# Revit family: Home collection grab rail - straight 900mm-687373C
name_source: partatom
category: Specialty Equipment
revit_build: Autodesk Revit 2015 (Build: 20140606_1530(x64)
units: mm (PartAtom-declared; Revit-internal decimal feet)

## types (8) — shared parameters
Assembly Code = C1030200
Default Elevation = 900 mm  [stored 2.95276 ft]
Manufacturer = GWA Bathrooms & Kitchens
URL = https://www.caroma.com.au

## per-type parameters (varying)
| type | Material_Rail | Model | Rail_Offset | Rail_Width |
| Home collection grab rail - straight 300mm Chrome | GWA_Metal-Chrome | 687370C | 76 mm  [stored 0.249344 ft] | 300 mm |
| Home collection grab rail - straight 300mm White | GWA-Metal-White | 687370W | 76 mm  [stored 0.249344 ft] | 300 mm |
| Home collection grab rail - straight 450mm Chrome | GWA_Metal-Chrome | 687371C | 76 mm  [stored 0.249344 ft] | 450 mm  [stored 1.47638 ft] |
| Home collection grab rail - straight 450mm White | GWA-Metal-White | 687371W | 76 mm  [stored 0.249344 ft] | 450 mm  [stored 1.47638 ft] |
| Home collection grab rail - straight 600mm Chrome | GWA_Metal-Chrome | 687372C | 71 mm  [stored 0.23294 ft] | 600 mm |
| Home collection grab rail - straight 600mm White | GWA-Metal-White | 687372W | 71 mm  [stored 0.23294 ft] | 600 mm |
| Home collection grab rail - straight 900mm Chrome | GWA_Metal-Chrome | 687373C | 71 mm  [stored 0.23294 ft] | 900 mm  [stored 2.95276 ft] |
| Home collection grab rail - straight 900mm White | GWA-Metal-White | 687373W | 71 mm  [stored 0.23294 ft] | 900 mm  [stored 2.95276 ft] |

note: column(s) folded — value = type name in every type: Description

note: [stored X ft] marks values corroborated as IEEE doubles in the binary element streams (Revit-internal decimal feet)

## geometry (parser evidence)
native form markers: Sweep x2
no freeform markers — native parametric forms only
